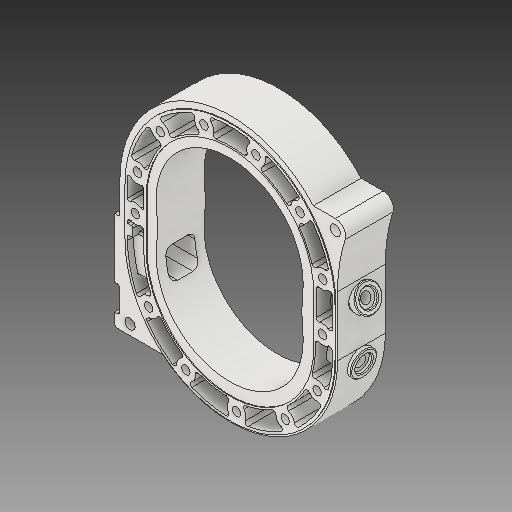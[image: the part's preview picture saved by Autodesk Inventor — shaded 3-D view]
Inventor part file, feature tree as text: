
AUTODESK INVENTOR PART (.ipt)
format: ipt  version: 2019 (Build 230136000, 136)  size: 673,280 bytes
history: native  units: in
note: dims shown in document units (in); Inventor stores cm internally (conversion verified against a paired STEP export)
features: thread x4, extrude x1, sketch x1, other x1
ambient origin geometry x8: Origin, YZ Plane, XZ Plane, XY Plane, X Axis, Y Axis, Z Axis, Center Point
bodies: Solid2 (feature_tree), Solid1 (feature_tree)
feature tree (7):
  thread  "Thread1"  [1 undecoded]
  thread  "Thread2"  [1 undecoded]
  thread  "Thread3"  [1 undecoded]
  thread  "Thread4"  [1 undecoded]
  extrude  "Extrusion2"  Depth=0.3937in TaperAngle=0.0deg
  sketch  "Sketch2"  dims[d14=0.0in d15=141.7323in d16=0.3937in d17=0.0in]
  other  "2D Equation Curve2"
note: 4 required parameter values undecoded (feature->parameter linkage not recoverable at this tier; creation-order binding heuristic only, values carry confidence <= 0.55)
